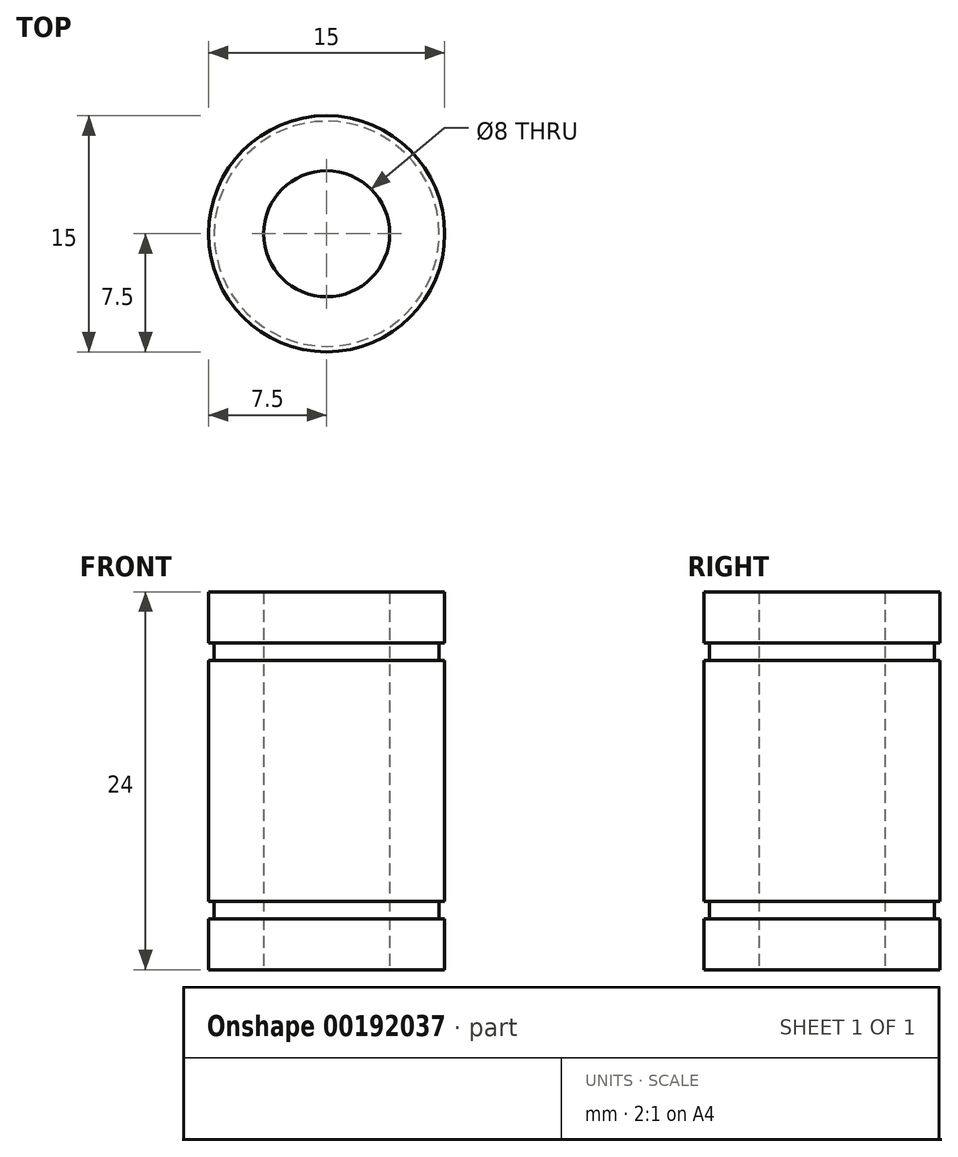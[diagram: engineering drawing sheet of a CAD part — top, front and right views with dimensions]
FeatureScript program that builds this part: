
annotation { "Feature Type Name" : "Feature", "Feature Type Description" : "" }
export const myFeature = defineFeature(function(context is Context, id is Id, definition is map)
    precondition{}
    {
        {
            var Q0;
            Q0=qCreatedBy(makeId("Front.planeOp"),FACE);
            var sketch = newSketch(context, id + "F0", { "sketchPlane" : qUnion([Q0])});
            skLineSegment(sketch, "E0.bottom", {"start": v(-4, -12) * mm, "end": v(-7.5, -12) * mm});
            skLineSegment(sketch, "E0.top", {"start": v(-4, 12) * mm, "end": v(-7.5, 12) * mm});
            skLineSegment(sketch, "E0.left", {"start": v(0, -12) * mm, "end": v(0, 12) * mm});
            skLineSegment(sketch, "E0.right", {"start": v(-7.5, -12) * mm, "end": v(-7.5, 12) * mm});
            skLineSegment(sketch, "E1", {"start": v(-4, 12) * mm, "end": v(-4, -12) * mm});
            skLineSegment(sketch, "E2.bottom", {"start": v(-7.5, 8.75) * mm, "end": v(-7.15, 8.75) * mm});
            skLineSegment(sketch, "E2.top", {"start": v(-7.5, 7.65) * mm, "end": v(-7.15, 7.65) * mm});
            skLineSegment(sketch, "E2.left", {"start": v(-7.5, 8.75) * mm, "end": v(-7.5, 7.65) * mm});
            skLineSegment(sketch, "E2.right", {"start": v(-7.15, 8.75) * mm, "end": v(-7.15, 7.65) * mm});
            skLineSegment(sketch, "E3", {"start": v(0, 0) * mm, "end": v(32.63, 0) * mm, "construction": true});
            skLineSegment(sketch, "E4.MirrorCS", {"start": v(-7.5, -7.65) * mm, "end": v(-7.15, -7.65) * mm});
            skLineSegment(sketch, "E5.MirrorCS", {"start": v(-7.5, -8.75) * mm, "end": v(-7.15, -8.75) * mm});
            skLineSegment(sketch, "E6.MirrorCS", {"start": v(-7.15, -8.75) * mm, "end": v(-7.15, -7.65) * mm});
            skSolve(sketch);
        }
        {
            var Q0;
            Q0=makeQuery(id+"F0.imprint","IMPRINT",FACE,{"disambiguationData":[TD([[makeQuery(id+"F0.imprint","IMPRINT",EDGE,{"derivedFrom":sQuery(id+"F0.wireOp",EDGE,"E0.bottom")}),-1.0]])]});
            var Q1;
            Q1=sQuery(id+"F0.wireOp",EDGE,"E0.left");
            revolve(context, id + "F1", {"entities" : qUnion([Q0]), "axis" : qUnion([Q1]), "revolveType" : RevolveType.FULL});
        }
    });
